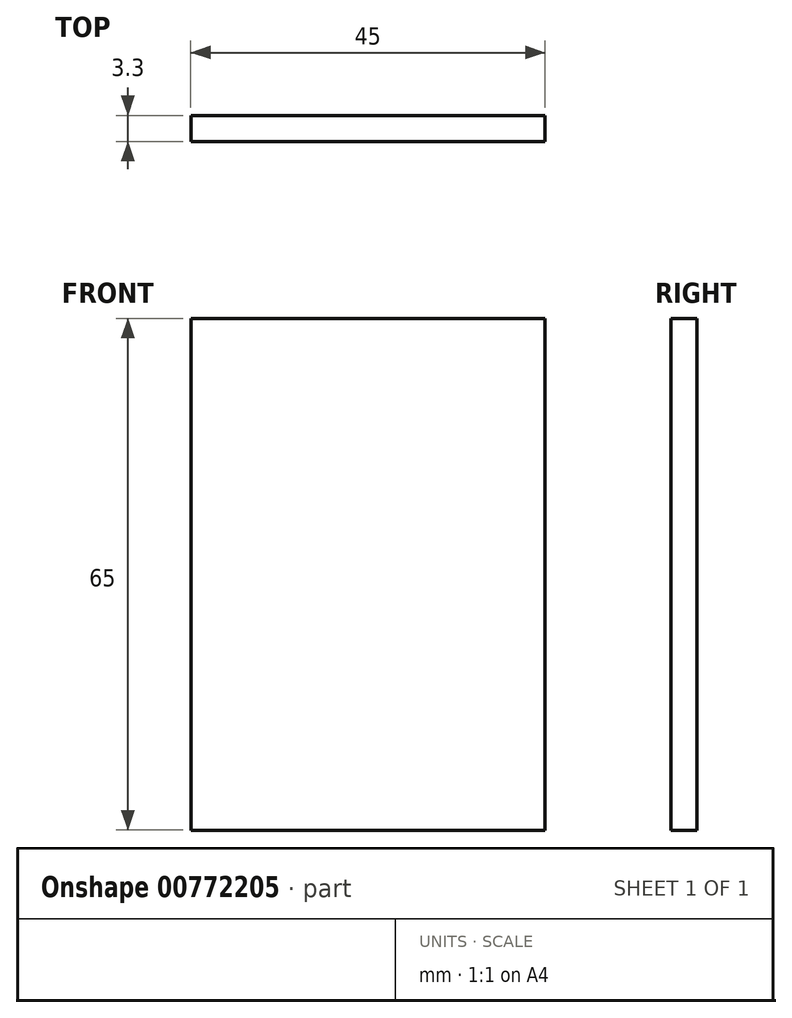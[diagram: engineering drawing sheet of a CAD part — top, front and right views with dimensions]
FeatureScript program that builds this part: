
annotation { "Feature Type Name" : "Feature", "Feature Type Description" : "" }
export const myFeature = defineFeature(function(context is Context, id is Id, definition is map)
    precondition{}
    {
        {
            var Q0;
            Q0=qCreatedBy(makeId("Front.planeOp"),FACE);
            var sketch = newSketch(context, id + "F0", { "sketchPlane" : qUnion([Q0])});
            skLineSegment(sketch, "E0.bottom", {"start": v(-39, 21.45) * mm, "end": v(6, 21.45) * mm});
            skLineSegment(sketch, "E0.top", {"start": v(-39, -43.55) * mm, "end": v(6, -43.55) * mm});
            skLineSegment(sketch, "E0.left", {"start": v(-39, 21.45) * mm, "end": v(-39, -43.55) * mm});
            skLineSegment(sketch, "E0.right", {"start": v(6, 21.45) * mm, "end": v(6, -43.55) * mm});
            skSolve(sketch);
        }
        {
            var Q0;
            Q0 = qSketchRegion(id + "F0", true);
            extrude(context, id + "F1", {"entities" : qUnion([Q0]), "depth" : 3.3 * mm, "offsetDistance" : 25 * mm});
        }
    });
